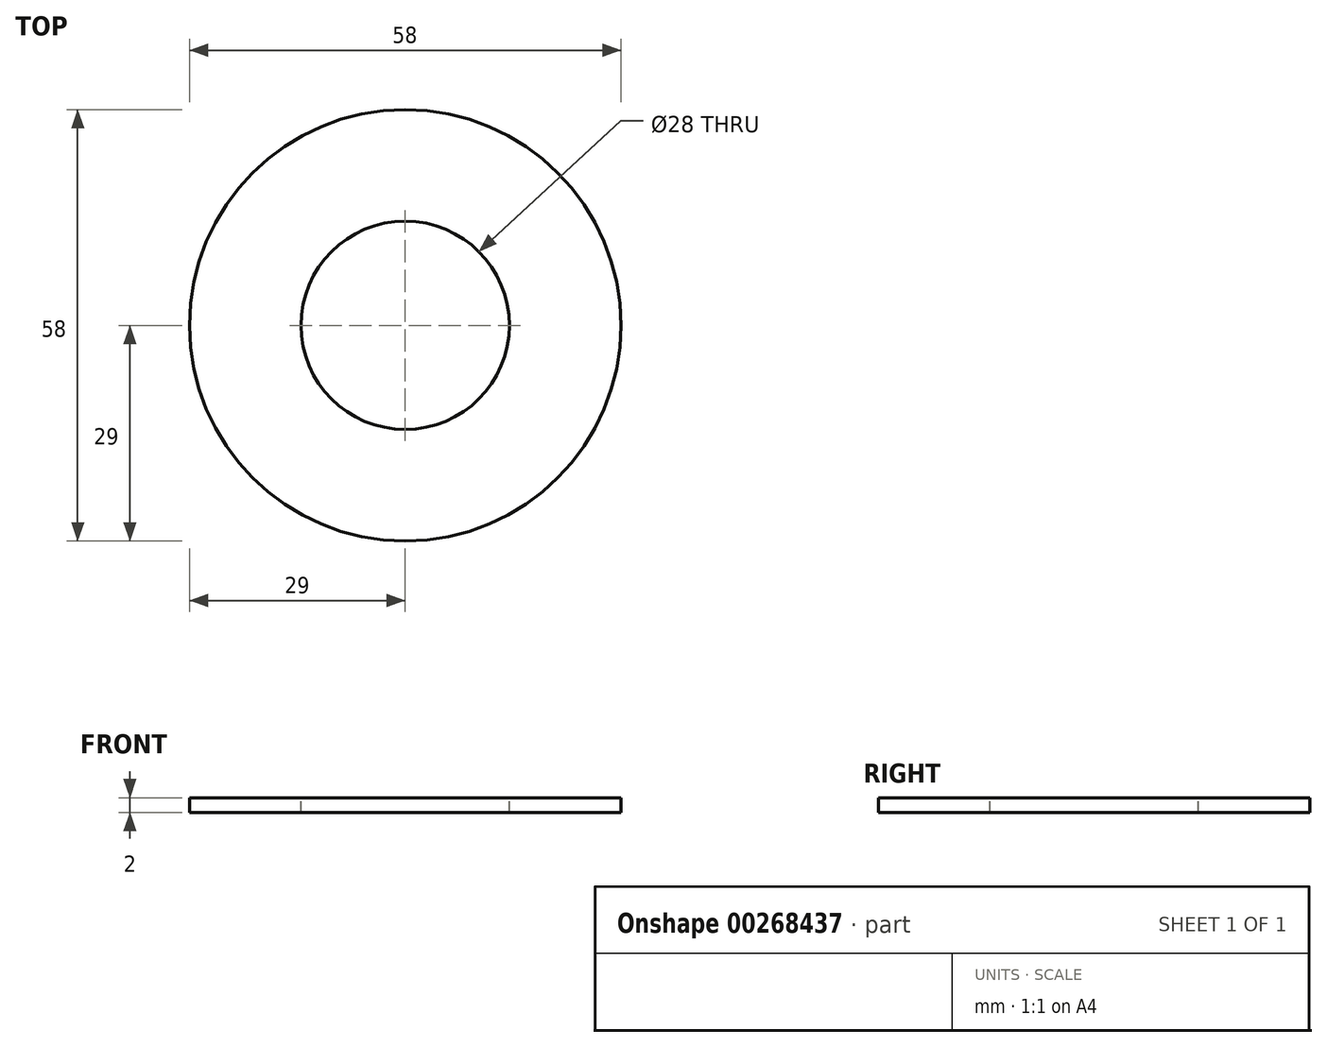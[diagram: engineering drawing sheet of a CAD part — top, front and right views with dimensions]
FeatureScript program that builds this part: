
annotation { "Feature Type Name" : "Feature", "Feature Type Description" : "" }
export const myFeature = defineFeature(function(context is Context, id is Id, definition is map)
    precondition{}
    {
        {
            var Q0;
            Q0=qCreatedBy(makeId("Top.planeOp"),FACE);
            var sketch = newSketch(context, id + "F0", { "sketchPlane" : qUnion([Q0])});
            skCircle(sketch, "E0", {"center": v(0, 0) * mm, "radius": 14 * mm});
            skCircle(sketch, "E1", {"center": v(0, 0) * mm, "radius": 29 * mm});
            skSolve(sketch);
        }
        {
            var Q0;
            Q0=makeQuery(id+"F0.imprint","IMPRINT",FACE,{"disambiguationData":[TD([[makeQuery(id+"F0.imprint","IMPRINT",EDGE,{"derivedFrom":sQuery(id+"F0.wireOp",EDGE,"E0")}),-1.0]])]});
            extrude(context, id + "F1", {"entities" : qUnion([Q0]), "oppositeDirection" : true, "depth" : 2 * mm});
        }
    });
